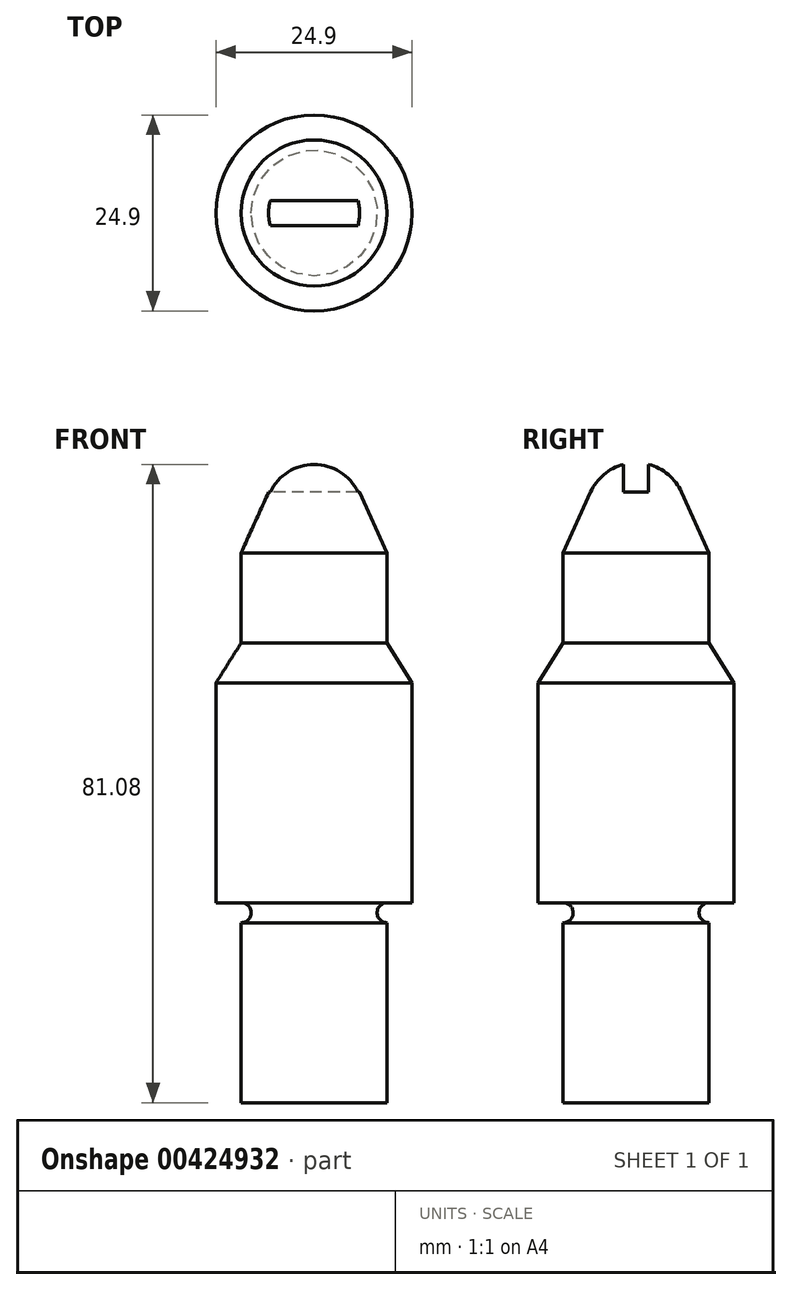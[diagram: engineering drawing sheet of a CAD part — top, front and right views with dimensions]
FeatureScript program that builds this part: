
annotation { "Feature Type Name" : "Feature", "Feature Type Description" : "" }
export const myFeature = defineFeature(function(context is Context, id is Id, definition is map)
    precondition{}
    {
        {
            var Q0;
            Q0=qCreatedBy(makeId("Front.planeOp"),FACE);
            var sketch = newSketch(context, id + "F0", { "sketchPlane" : qUnion([Q0])});
            skLineSegment(sketch, "E0", {"start": v(0, 0) * mm, "end": v(0, 81.28) * mm});
            skLineSegment(sketch, "E1", {"start": v(0, 0) * mm, "end": v(-9.27, 0) * mm});
            skLineSegment(sketch, "E2", {"start": v(-9.27, 0) * mm, "end": v(-9.27, 22.86) * mm});
            skLineSegment(sketch, "E3", {"start": v(-9.27, 25.4) * mm, "end": v(-12.45, 25.4) * mm});
            skLineSegment(sketch, "E4", {"start": v(-12.45, 25.4) * mm, "end": v(-12.45, 53.34) * mm});
            skLineSegment(sketch, "E5", {"start": v(-12.45, 53.34) * mm, "end": v(-9.27, 58.42) * mm});
            skLineSegment(sketch, "E6", {"start": v(-9.27, 58.42) * mm, "end": v(-9.27, 69.85) * mm});
            skLineSegment(sketch, "E7", {"start": v(-9.27, 69.85) * mm, "end": v(-5.78, 77.55) * mm});
            skArc(sketch, "E8", {"start": v(0, 81.28) * mm, "mid": v(-3.44, 80.27) * mm, "end": v(-5.78, 77.55) * mm});
            skArc(sketch, "E9", {"start": v(-9.27, 22.86) * mm, "mid": v(-8, 24.13) * mm, "end": v(-9.27, 25.4) * mm});
            skSolve(sketch);
        }
        {
            var Q0;
            Q0 = qSketchRegion(id + "F0", true);
            var Q1;
            Q1=sQuery(id+"F0.wireOp",EDGE,"E0");
            revolve(context, id + "F1", {"entities" : qUnion([Q0]), "axis" : qUnion([Q1]), "revolveType" : RevolveType.FULL});
        }
        {
            var Q0;
            Q0=qCreatedBy(makeId("Front.planeOp"),FACE);
            var sketch = newSketch(context, id + "F2", { "sketchPlane" : qUnion([Q0])});
            skLineSegment(sketch, "E10.0", {"start": v(5.78, 77.55) * mm, "end": v(-5.78, 77.55) * mm});
            skArc(sketch, "E11", {"start": v(5.78, 77.55) * mm, "mid": v(0, 81.28) * mm, "end": v(-5.78, 77.55) * mm});
            skArc(sketch, "E12.0", {"start": v(0, 81.28) * mm, "mid": v(-3.44, 80.27) * mm, "end": v(-5.78, 77.55) * mm});
            skSolve(sketch);
        }
        {
            var Q0;
            Q0 = qSketchRegion(id + "F2", true);
            extrude(context, id + "F3", {"entities" : qUnion([Q0]), "operationType" : NewBodyOperationType.REMOVE, "oppositeDirection" : true, "depth" : 3.17 * mm, "symmetric" : true});
        }
    });
